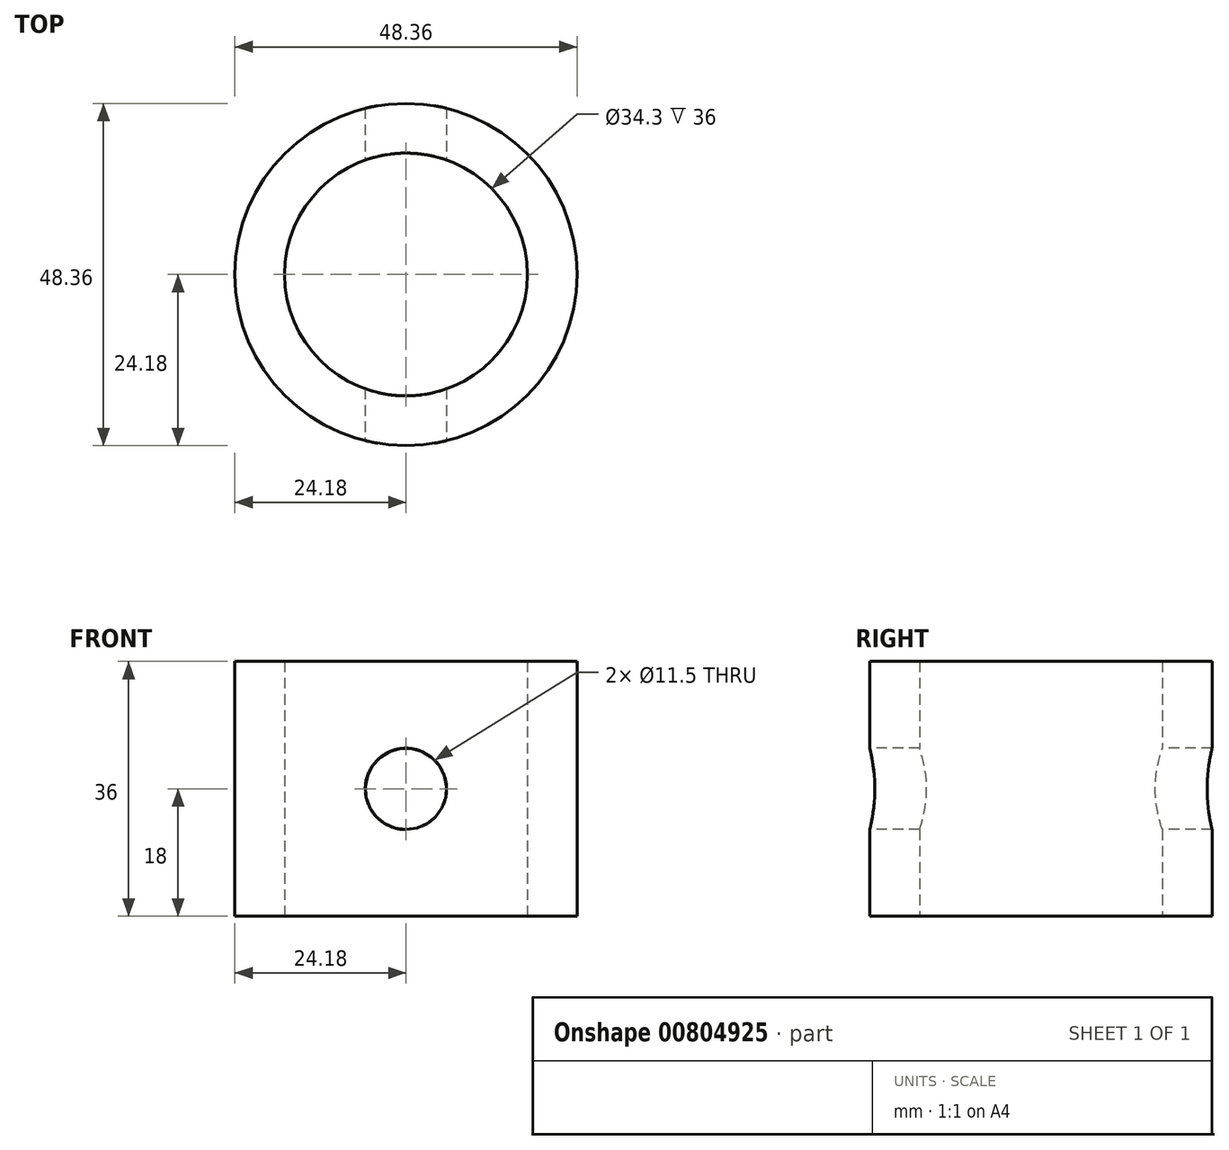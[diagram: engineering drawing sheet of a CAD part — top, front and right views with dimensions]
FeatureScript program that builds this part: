
annotation { "Feature Type Name" : "Feature", "Feature Type Description" : "" }
export const myFeature = defineFeature(function(context is Context, id is Id, definition is map)
    precondition{}
    {
        {
            var Q0;
            Q0=qCreatedBy(makeId("Top.planeOp"),FACE);
            var sketch = newSketch(context, id + "F0", { "sketchPlane" : qUnion([Q0])});
            skCircle(sketch, "E0", {"center": v(0, 0) * mm, "radius": 17.15 * mm});
            skCircle(sketch, "E1", {"center": v(0, 0) * mm, "radius": 24.18 * mm});
            skSolve(sketch);
        }
        {
            var Q0;
            Q0 = qSketchRegion(id + "F0", true);
            extrude(context, id + "F1", {"entities" : qUnion([Q0]), "endBound" : BoundingType.SYMMETRIC, "depth" : 36 * mm, "offsetDistance" : 25.4 * mm});
        }
        {
            var Q0;
            Q0=qCreatedBy(makeId("Front.planeOp"),FACE);
            var sketch = newSketch(context, id + "F2", { "sketchPlane" : qUnion([Q0])});
            skCircle(sketch, "E2", {"center": v(0, 0) * mm, "radius": 5.75 * mm});
            skSolve(sketch);
        }
        {
            var Q0;
            Q0 = qSketchRegion(id + "F2", true);
            extrude(context, id + "F3", {"entities" : qUnion([Q0]), "operationType" : NewBodyOperationType.REMOVE, "endBound" : BoundingType.SYMMETRIC, "oppositeDirection" : true, "depth" : 1295.4 * mm, "offsetDistance" : 25.4 * mm});
        }
    });
